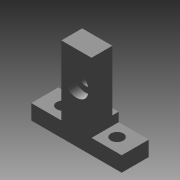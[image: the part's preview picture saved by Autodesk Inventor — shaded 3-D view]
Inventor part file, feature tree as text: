
AUTODESK INVENTOR PART (.ipt)
format: ipt  version: 2015 SP1 (Build 190203100, 203)  size: 116,736 bytes
history: native  units: mm
features: extrude x5, sketch x4
ambient origin geometry x8: Origin, YZ Plane, XZ Plane, XY Plane, X Axis, Y Axis, Z Axis, Center Point
bodies: Solid1 (feature_tree)
feature tree (9):
  extrude  "Extrusion1"  Depth=30.0mm
  extrude  "Extrusion2"  Depth=5.0mm
  extrude  "Extrusion3"  Depth=4.5mm
  sketch  "Sketch4"  dims[d7=10.0mm d8=3.0mm d9=0.0mm d10=6.9mm d11=20.0mm d12=0.0mm d13=8.0mm d14=4.125mm d15=3.0mm d16=0.0mm d17=3.0mm d18=0.0mm d19=10.0mm]
  extrude  "Extrusion4"  Depth=3.0mm TaperAngle=0.0deg
  extrude  "Extrusion5"  Depth=6.9mm
  sketch  "Sketch1"  dims[d0=9.0mm d1=30.0mm]
  sketch  "Sketch2"  dims[d2=5.0mm d3=0.0mm d4=4.125mm]
  sketch  "Sketch3"  dims[d5=6.0mm d6=4.5mm]
